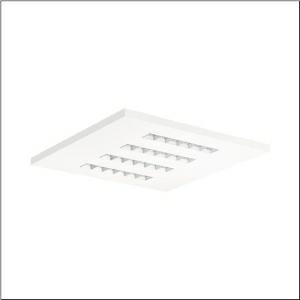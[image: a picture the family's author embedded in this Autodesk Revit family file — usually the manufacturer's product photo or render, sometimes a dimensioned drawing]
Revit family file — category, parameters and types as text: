
# Revit family: silica_r__21_square_51mx6mds44w_aad7
name_source: partatom
category: Lighting Fixtures
units: mm (PartAtom-declared; Revit-internal decimal feet)

## family parameters
Cut with Voids When Loaded = No
Host = Face
Light Source = No
Part Type = Normal
Room Calculation Point = No
Round Connector Dimension = Use Diameter
Shared = No

## types (1)
- --- (1 x LED, 4600 lm, 27.2 W, 4000K)
    Apparent Load = 27 VA
    CIE Flux Codes = 83 98 100 100 100
    Color Rendering = 80
    Color Temperature = 4000K
    Default Elevation = 1800 mm
    Description = Silica® 21 Square, office luminaire, primary light control with lens, of PMMA, primary anti-glare with reflector, of PC, white, CAT 2 (L<= 3000cd/m²), light emission: direct distribution, primary light characteristic: symmetric, installation type: lay-in mounting, LED, rated luminous flux: 4.600lm, luminous efficacy: 169lm/W, light colour: 840, colour temperature: 4000K, control gear: DALI 2, with terminal, 5-pole, mains connection: 220..240V, AC, 50/60Hz, rated input power: 27.2W, luminaire housing, of sheet steel, coated, traffic white (RAL 9016), module: M600, length: 597mm, width: 597mm, height: 33mm, protection rating (complete): IP20, insulation class (complete): insulation class I (protective earthing), certification: CE, ENEC, VDE, permissible operating ambient temperature: -20..+40°C, standard: EN 50419, packaging unit: 1 piece
    Height = 0 mm  [stored 0 ft]
    Lamp = 1 x LED
    Lamp Light Flux = 4600 lm
    Lamp Power = 27.2 W
    Lamp count = 1
    Length = 597 mm
    Luminous efficacy = 169 lm/W
    Manufacturer = Siteco
    ModVariant = No
    Model = 51MX6MDS44W
    Mounting Place = Ceiling
    Mounting Type = Recessed
    Number of Poles = 1
    OnlyDefault = Yes
    Power Factor = 1
    Product Name = Silica® 21 Square
    Product group = office luminaire | ceiling recessed
    ProductGroupID = 400
    Protection Class = Protection class I
    Protection Degree = IP 20
    RLX_Detail_Level = 1
    RLX_Emergency_Light_Flux = 0 lm
    RLX_Emergency_Type = 0
    RLX_Emergency_Type_DB = No
    RlxData = <blob elided: 18629 chars, md5=b695d621>
    Socket = socket
    Standby Power = 0 W
    System Light Flux = 4600 lm
    System Power = 27 W
    Type Comments = factory setting: luminous flux: 100 % | dim-lin: 254 | 366 mA
    Type Image = l_1275220.jpg
    URL = http://relux.com
    VarID = @adj_105299
    Voltage = 0 V
    Weight = 0.00 kg
    Width = 597 mm

note: [stored X ft] marks values corroborated as IEEE doubles in the binary element streams (Revit-internal decimal feet)

## geometry (parser evidence)
native form markers: Blend x4, Sweep x11
no freeform markers — native parametric forms only
